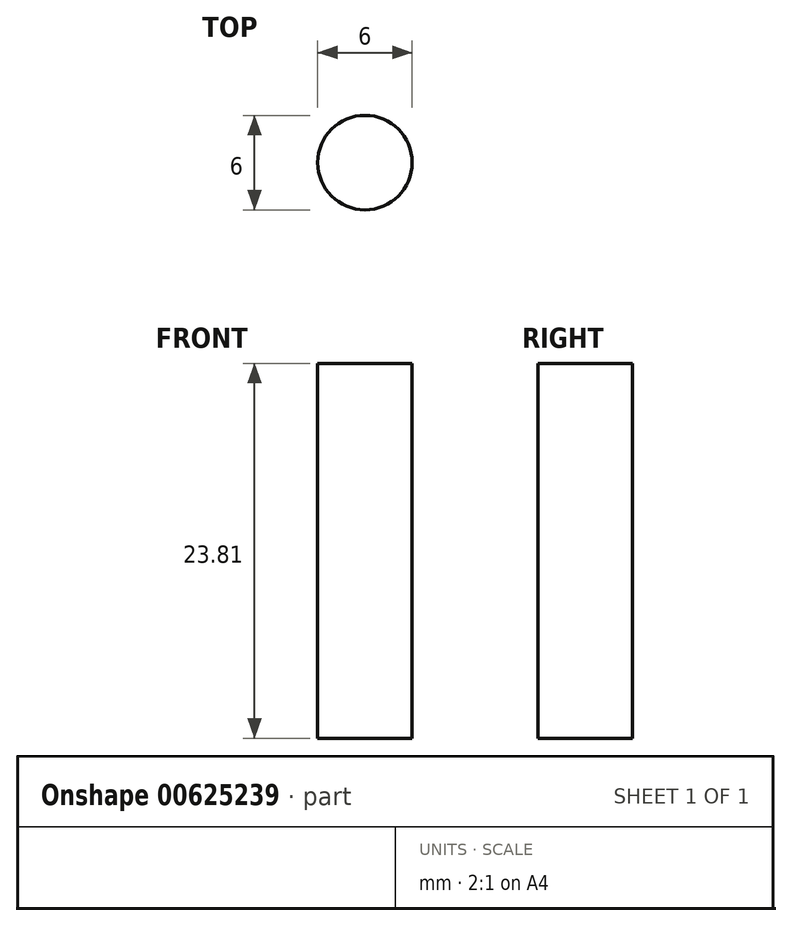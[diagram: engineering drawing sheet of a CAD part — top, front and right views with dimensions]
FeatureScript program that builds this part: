
annotation { "Feature Type Name" : "Feature", "Feature Type Description" : "" }
export const myFeature = defineFeature(function(context is Context, id is Id, definition is map)
    precondition{}
    {
        {
            var Q0;
            Q0=qCreatedBy(makeId("Top.planeOp"),FACE);
            var sketch = newSketch(context, id + "F0", { "sketchPlane" : qUnion([Q0])});
            skCircle(sketch, "E0", {"center": v(0, 0) * mm, "radius": 3 * mm});
            skSolve(sketch);
        }
        {
            var Q0;
            Q0 = qSketchRegion(id + "F0", true);
            extrude(context, id + "F1", {"entities" : qUnion([Q0]), "depth" : 23.8 * mm, "offsetDistance" : 25.4 * mm});
        }
    });
